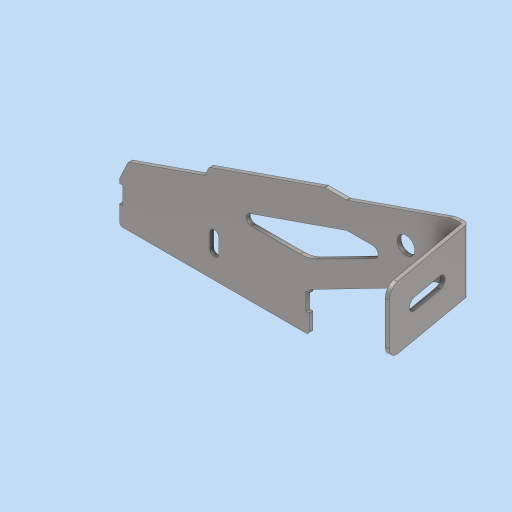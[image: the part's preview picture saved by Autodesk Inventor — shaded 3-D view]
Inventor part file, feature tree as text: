
AUTODESK INVENTOR PART (.ipt)
format: ipt  version: 2023 (Build 270158000, 158)  size: 221,184 bytes
history: native  units: mm
features: other x4, sketch x1, plane x1
ambient origin geometry x8: Origin, YZ Plane, XZ Plane, XY Plane, X Axis, Y Axis, Z Axis, Center Point
bodies: Body1 (feature_tree)
feature tree (6):
  other  "吊架-短(R) - 焊接件-1(v220714).ipt"
  other  "實體1::吊架-短(R) - 焊接件-1(v220714).ipt"
  other  "標籤特徵1"
  sketch  "草圖1"
  plane  "工作平面1"
  other  "實體1"
